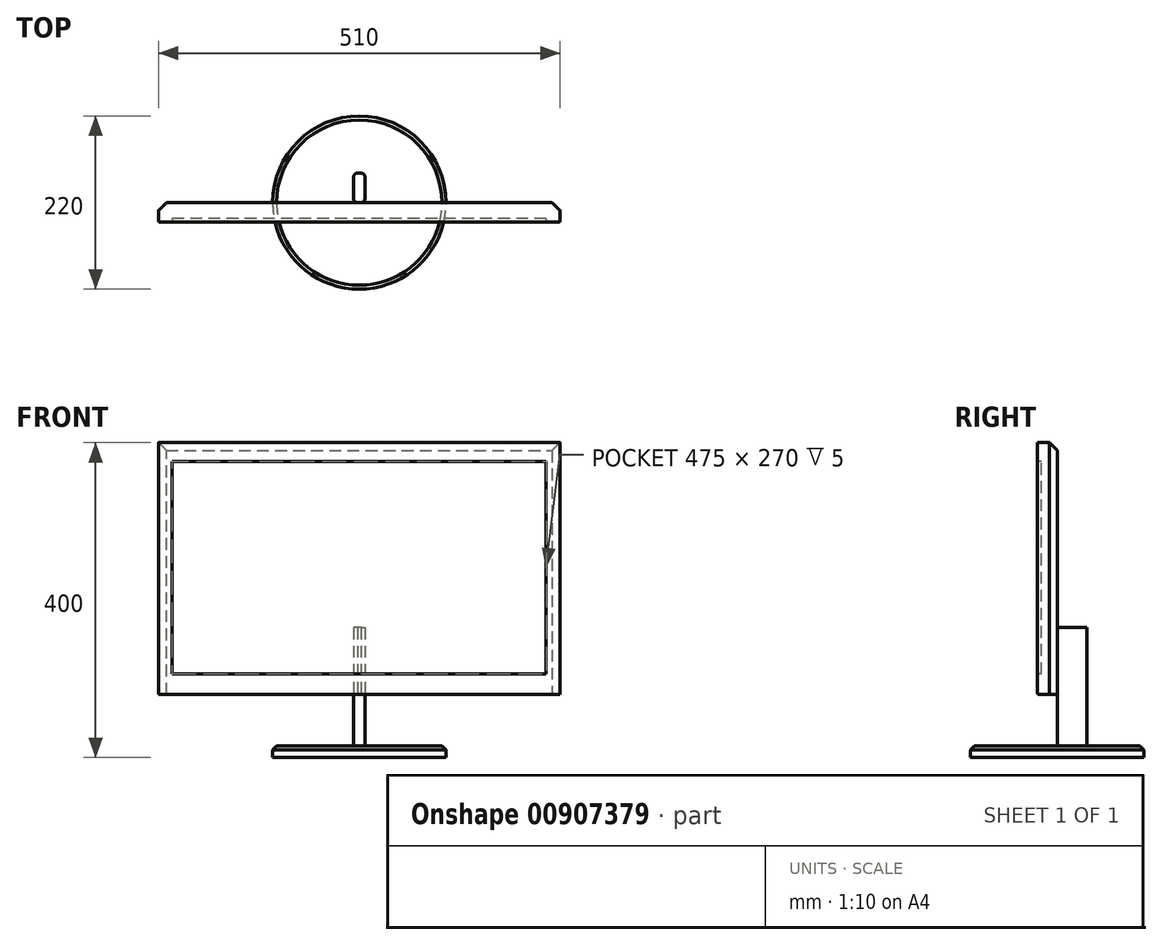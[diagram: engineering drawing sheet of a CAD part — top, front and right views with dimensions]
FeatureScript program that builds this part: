
annotation { "Feature Type Name" : "Feature", "Feature Type Description" : "" }
export const myFeature = defineFeature(function(context is Context, id is Id, definition is map)
    precondition{}
    {
        {
            var Q0;
            Q0=qCreatedBy(makeId("Top.planeOp"),FACE);
            var sketch = newSketch(context, id + "F0", { "sketchPlane" : qUnion([Q0])});
            skCircle(sketch, "E0", {"center": v(0, 0) * mm, "radius": 110 * mm});
            skSolve(sketch);
        }
        {
            var Q0;
            Q0=makeQuery(id+"F0.imprint","IMPRINT",FACE,{"disambiguationData":[TD([[makeQuery(id+"F0.imprint","IMPRINT",EDGE,{"derivedFrom":sQuery(id+"F0.wireOp",EDGE,"E0")}),1.0]])]});
            extrude(context, id + "F1", {"entities" : qUnion([Q0]), "depth" : 15 * mm, "offsetDistance" : 25 * mm});
        }
        {
            var Q0;
            Q0=makeQuery(id+"F1.opExtrude","CAP_EDGE",EDGE,{"disambiguationData":[OSD([sQuery(id+"F0.wireOp",EDGE,"E0")])],"isStart":false});
            chamfer(context, id + "F2", {"entities" : qUnion([Q0]), "width" : 5 * mm, "tangentPropagation" : true});
        }
        {
            var Q0;
            Q0=makeQuery(id+"F1.opExtrude","CAP_FACE",FACE,{"disambiguationData":[OSD([sQuery(id+"F0.wireOp",EDGE,"E0")])],"isStart":false});
            var sketch = newSketch(context, id + "F3", { "sketchPlane" : qUnion([Q0])});
            skLineSegment(sketch, "E1.bottom", {"start": v(7.24, 37.4) * mm, "end": v(-7.24, 37.4) * mm});
            skLineSegment(sketch, "E1.top", {"start": v(7.24, 0) * mm, "end": v(-7.24, 0) * mm});
            skLineSegment(sketch, "E1.left", {"start": v(7.24, 37.4) * mm, "end": v(7.24, 0) * mm});
            skLineSegment(sketch, "E1.right", {"start": v(-7.24, 37.4) * mm, "end": v(-7.24, 0) * mm});
            skPoint(sketch, "E1.middle", {"position": v(0, 18.7) * mm});
            skSolve(sketch);
        }
        {
            var Q0;
            Q0 = qSketchRegion(id + "F3", true);
            extrude(context, id + "F4", {"entities" : qUnion([Q0]), "operationType" : NewBodyOperationType.ADD, "depth" : 150 * mm, "offsetDistance" : 25 * mm});
        }
        {
            var Q0;
            Q0=makeQuery(id+"F4.opExtrude","SWEPT_EDGE",EDGE,{"disambiguationData":[OSD([sQuery(id+"F3.wireOp",EDGE,"E1.top"),sQuery(id+"F3.wireOp",EDGE,"E1.right")])]});
            var Q1;
            Q1=makeQuery(id+"F4.opExtrude","SWEPT_EDGE",EDGE,{"disambiguationData":[OSD([sQuery(id+"F3.wireOp",EDGE,"E1.top"),sQuery(id+"F3.wireOp",EDGE,"E1.left")])]});
            var Q2;
            Q2=makeQuery(id+"F4.opExtrude","SWEPT_EDGE",EDGE,{"disambiguationData":[OSD([sQuery(id+"F3.wireOp",EDGE,"E1.bottom"),sQuery(id+"F3.wireOp",EDGE,"E1.left")])]});
            var Q3;
            Q3=makeQuery(id+"F4.opExtrude","SWEPT_EDGE",EDGE,{"disambiguationData":[OSD([sQuery(id+"F3.wireOp",EDGE,"E1.bottom"),sQuery(id+"F3.wireOp",EDGE,"E1.right")])]});
            fillet(context, id + "F5", {"entities" : qUnion([Q0, Q1, Q2, Q3]), "radius" : 5 * mm, "tangentPropagation" : true, "allowEdgeOverflow" : false});
        }
        {
            var Q0;
            Q0=makeQuery(id+"F4.opExtrude","SWEPT_FACE",FACE,{"disambiguationData":[OSD([sQuery(id+"F3.wireOp",EDGE,"E1.top")])]});
            var sketch = newSketch(context, id + "F6", { "sketchPlane" : qUnion([Q0])});
            skLineSegment(sketch, "E2.bottom", {"start": v(255, 80) * mm, "end": v(-255, 80) * mm});
            skLineSegment(sketch, "E2.top", {"start": v(255, 400) * mm, "end": v(-255, 400) * mm});
            skLineSegment(sketch, "E2.left", {"start": v(255, 80) * mm, "end": v(255, 400) * mm});
            skLineSegment(sketch, "E2.right", {"start": v(-255, 80) * mm, "end": v(-255, 400) * mm});
            skPoint(sketch, "E2.middle", {"position": v(0, 240) * mm});
            skSolve(sketch);
        }
        {
            var Q0;
            Q0 = qSketchRegion(id + "F6", true);
            extrude(context, id + "F7", {"entities" : qUnion([Q0]), "operationType" : NewBodyOperationType.ADD, "depth" : 25 * mm, "offsetDistance" : 25 * mm});
        }
        {
            var Q0;
            Q0=makeQuery(id+"F7.opExtrude","CAP_EDGE",EDGE,{"disambiguationData":[OSD([sQuery(id+"F6.wireOp",EDGE,"E2.right")])],"isStart":true});
            var Q1;
            Q1=makeQuery(id+"F7.opExtrude","CAP_EDGE",EDGE,{"disambiguationData":[OSD([sQuery(id+"F6.wireOp",EDGE,"E2.top")])],"isStart":true});
            var Q2;
            Q2=makeQuery(id+"F7.opExtrude","CAP_EDGE",EDGE,{"disambiguationData":[OSD([sQuery(id+"F6.wireOp",EDGE,"E2.left")])],"isStart":true});
            chamfer(context, id + "F8", {"entities" : qUnion([Q0, Q1, Q2]), "width" : 10 * mm, "tangentPropagation" : true});
        }
        {
            var Q0;
            Q0=makeQuery(id+"F7.opExtrude","CAP_EDGE",EDGE,{"disambiguationData":[OSD([sQuery(id+"F6.wireOp",EDGE,"E2.right")])],"isStart":false});
            var Q1;
            Q1=makeQuery(id+"F7.opExtrude","CAP_EDGE",EDGE,{"disambiguationData":[OSD([sQuery(id+"F6.wireOp",EDGE,"E2.bottom")])],"isStart":false});
            var Q2;
            Q2=makeQuery(id+"F7.opExtrude","CAP_EDGE",EDGE,{"disambiguationData":[OSD([sQuery(id+"F6.wireOp",EDGE,"E2.left")])],"isStart":false});
            var Q3;
            {var subQ0=sQuery(id+"F6.wireOp",EDGE,"E2.top");Q3=makeQuery(id+"F8.opChamfer","BLEND_EDGE",EDGE,{"blendedFrom":[makeQuery(id+"F7.opExtrude","CAP_EDGE",EDGE,{"disambiguationData":[OSD([subQ0])],"isStart":true}),makeQuery(id+"F7.opExtrude","SWEPT_FACE",FACE,{"disambiguationData":[OSD([subQ0])]})],"blendedInto":[makeQuery(id+"F7.opExtrude","SWEPT_FACE",FACE,{"disambiguationData":[OSD([subQ0])]})]});}
            fillet(context, id + "F9", {"entities" : qUnion([Q0, Q1, Q2, Q3]), "radius" : 2 * mm, "tangentPropagation" : true, "allowEdgeOverflow" : false});
        }
        {
            var Q0;
            Q0=makeQuery(id+"F7.opExtrude","CAP_FACE",FACE,{"disambiguationData":[OSD([sQuery(id+"F6.wireOp",EDGE,"E2.bottom"),sQuery(id+"F6.wireOp",EDGE,"E2.top"),sQuery(id+"F6.wireOp",EDGE,"E2.left"),sQuery(id+"F6.wireOp",EDGE,"E2.right")])],"isStart":false});
            var sketch = newSketch(context, id + "F10", { "sketchPlane" : qUnion([Q0])});
            skLineSegment(sketch, "E3.bottom", {"start": v(237.5, 106) * mm, "end": v(-237.5, 106) * mm});
            skLineSegment(sketch, "E3.top", {"start": v(237.5, 376) * mm, "end": v(-237.5, 376) * mm});
            skLineSegment(sketch, "E3.left", {"start": v(237.5, 106) * mm, "end": v(237.5, 376) * mm});
            skLineSegment(sketch, "E3.right", {"start": v(-237.5, 106) * mm, "end": v(-237.5, 376) * mm});
            skPoint(sketch, "E3.middle", {"position": v(0, 241) * mm});
            skPoint(sketch, "E3.middle.positionSnap0", {"position": v(253, 241) * mm});
            skPoint(sketch, "E3.centerSnap0", {"position": v(253, 241) * mm});
            skSolve(sketch);
        }
        {
            var Q0;
            Q0 = qSketchRegion(id + "F10", true);
            extrude(context, id + "F11", {"entities" : qUnion([Q0]), "operationType" : NewBodyOperationType.REMOVE, "oppositeDirection" : true, "depth" : 5 * mm, "offsetDistance" : 25 * mm});
        }
    });
